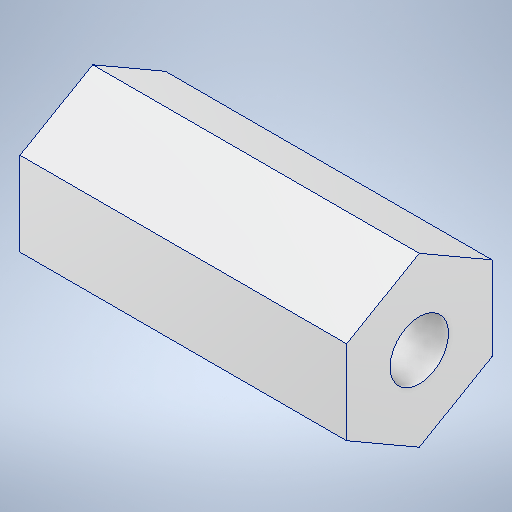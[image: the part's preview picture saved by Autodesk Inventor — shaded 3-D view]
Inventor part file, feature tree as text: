
AUTODESK INVENTOR PART (.ipt)
format: ipt  version: 2025.1 (Build 291241020, 241B)  size: 215,552 bytes
history: native  units: in
note: dims shown in document units (in); Inventor stores cm internally (conversion verified against a paired STEP export)
features: extrude x1, sketch x1
ambient origin geometry x8: Origin, YZ Plane, XZ Plane, XY Plane, X Axis, Y Axis, Z Axis, Center Point
bodies: Solid1 (feature_tree)
feature tree (2):
  extrude  "Extrusion1"  Depth=1.123in TaperAngle=0.0deg
  sketch  "Sketch1"  dims[d1=0.5in d3=1.123in d4=0.0in d5=0.201in]
